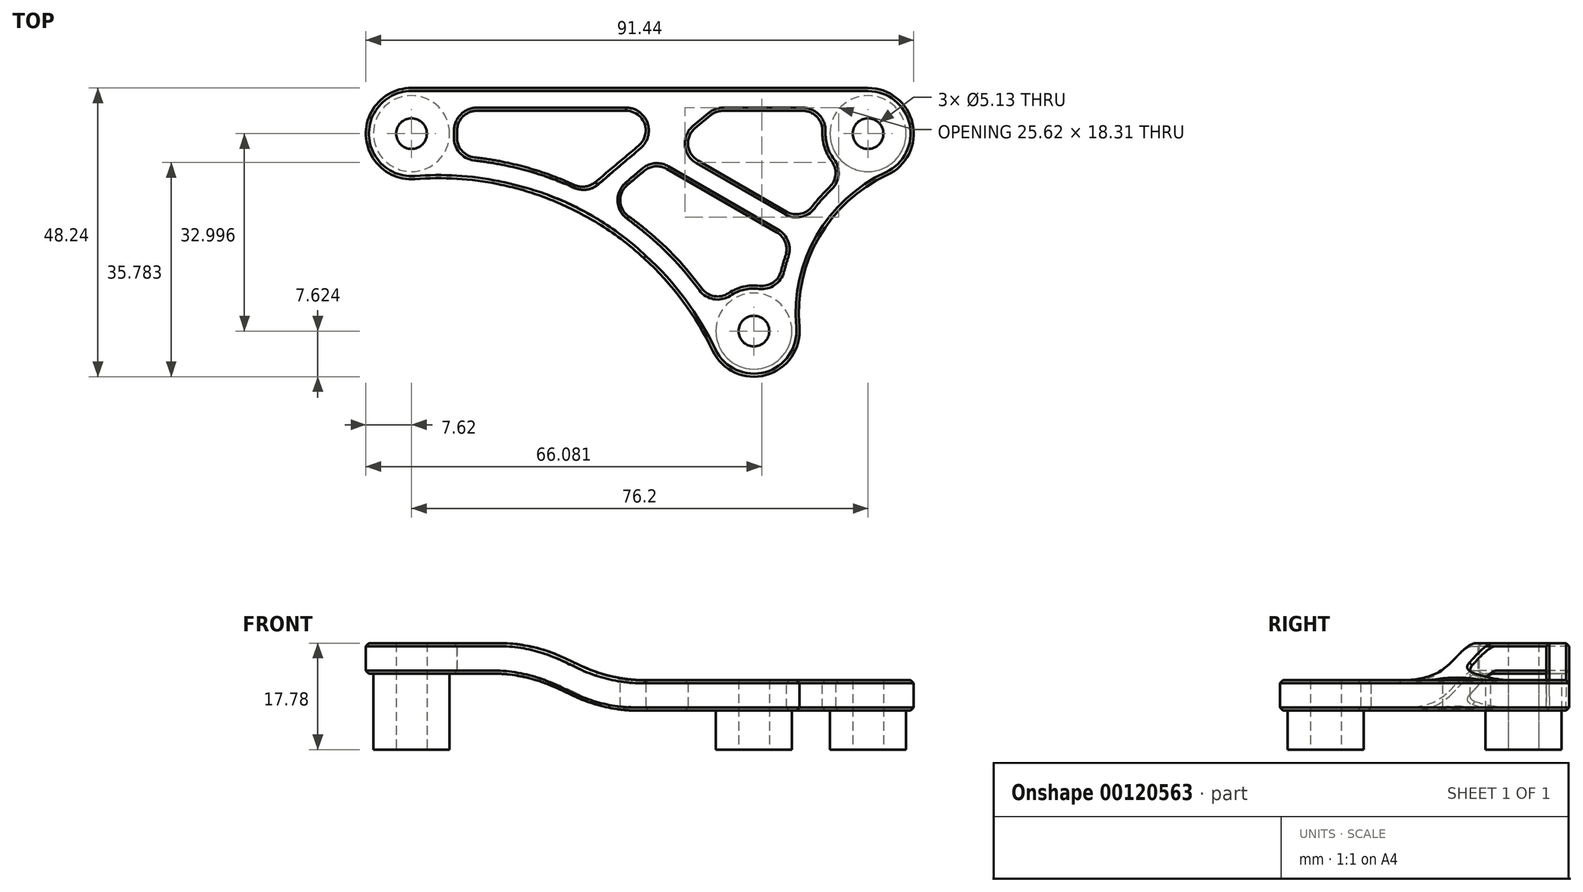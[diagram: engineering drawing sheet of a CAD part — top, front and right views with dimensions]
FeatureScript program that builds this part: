
annotation { "Feature Type Name" : "Feature", "Feature Type Description" : "" }
export const myFeature = defineFeature(function(context is Context, id is Id, definition is map)
    precondition{}
    {
        {
            var Q0;
            Q0=qCreatedBy(makeId("Top.planeOp"),FACE);
            var sketch = newSketch(context, id + "F0", { "sketchPlane" : qUnion([Q0])});
            skCircle(sketch, "E0", {"center": v(0, 0) * mm, "radius": 6.35 * mm});
            skCircle(sketch, "E1", {"center": v(76.2, 0) * mm, "radius": 6.35 * mm, "construction": true});
            skCircle(sketch, "E2", {"center": v(57.15, -33) * mm, "radius": 6.35 * mm, "construction": true});
            skLineSegment(sketch, "E3", {"start": v(0, 0) * mm, "end": v(76.2, 0) * mm, "construction": true});
            skLineSegment(sketch, "E4", {"start": v(57.15, -33) * mm, "end": v(76.2, 0) * mm, "construction": true});
            skSolve(sketch);
        }
        {
            var Q0;
            Q0 = qSketchRegion(id + "F0", true);
            extrude(context, id + "F1", {"entities" : qUnion([Q0]), "depth" : 17.78 * mm});
        }
        {
            var Q0;
            Q0=makeQuery(id+"F0.imprint","IMPRINT",FACE,{"disambiguationData":[TD([[makeQuery(id+"F0.imprint","IMPRINT",EDGE,{"derivedFrom":sQuery(id+"F0.wireOp",EDGE,"E0")}),1.0]])]});
            var sketch = newSketch(context, id + "F2", { "sketchPlane" : qUnion([Q0])});
            skCircle(sketch, "E5.0", {"center": v(76.2, 0) * mm, "radius": 6.35 * mm});
            skCircle(sketch, "E5.1", {"center": v(57.15, -33) * mm, "radius": 6.35 * mm});
            skSolve(sketch);
        }
        {
            var Q0;
            Q0 = qSketchRegion(id + "F2", true);
            extrude(context, id + "F3", {"entities" : qUnion([Q0]), "depth" : 7.62 * mm});
        }
        {
            var Q0;
            Q0=qCreatedBy(makeId("Front.planeOp"),FACE);
            var sketch = newSketch(context, id + "F4", { "sketchPlane" : qUnion([Q0])});
            skLineSegment(sketch, "E6", {"start": v(-12.8, 17.78) * mm, "end": v(20.18, 17.78) * mm});
            skLineSegment(sketch, "E7", {"start": v(84.3, 11.57) * mm, "end": v(33.5, 11.57) * mm});
            skLineSegment(sketch, "E8", {"start": v(20.18, 17.78) * mm, "end": v(33.5, 11.57) * mm});
            skLineSegment(sketch, "E9.0", {"start": v(84.3, 6.49) * mm, "end": v(32.37, 6.49) * mm});
            skLineSegment(sketch, "E9.1", {"start": v(19.05, 12.7) * mm, "end": v(32.37, 6.49) * mm});
            skLineSegment(sketch, "E9.2", {"start": v(-12.8, 12.7) * mm, "end": v(19.05, 12.7) * mm});
            skLineSegment(sketch, "E10", {"start": v(-12.8, 17.78) * mm, "end": v(-12.8, 12.7) * mm});
            skLineSegment(sketch, "E11", {"start": v(84.3, 6.49) * mm, "end": v(84.3, 11.57) * mm});
            skSolve(sketch);
        }
        {
            var Q0;
            Q0 = qSketchRegion(id + "F4", true);
            extrude(context, id + "F5", {"entities" : qUnion([Q0]), "operationType" : NewBodyOperationType.ADD, "depth" : 40.64 * mm, "hasSecondDirection" : true, "secondDirectionOppositeDirection" : true, "secondDirectionDepth" : 12.7 * mm});
        }
        {
            var Q0;
            Q0=qCreatedBy(makeId("Top.planeOp"),FACE);
            var sketch = newSketch(context, id + "F6", { "sketchPlane" : qUnion([Q0])});
            skArc(sketch, "E12", {"start": v(50.28, -36.29) * mm, "mid": v(29.87, -14.25) * mm, "end": v(0.58, -7.6) * mm});
            skArc(sketch, "E13", {"start": v(0, 7.62) * mm, "mid": v(-7.61, -0.3) * mm, "end": v(0.58, -7.6) * mm});
            skArc(sketch, "E14", {"start": v(50.28, -36.29) * mm, "mid": v(59.18, -40.34) * mm, "end": v(64.74, -32.3) * mm});
            skArc(sketch, "E15", {"start": v(79.4, -6.92) * mm, "mid": v(83.64, 1.63) * mm, "end": v(76.2, 7.62) * mm});
            skLineSegment(sketch, "E16", {"start": v(0, 7.62) * mm, "end": v(76.2, 7.62) * mm});
            skArc(sketch, "E17", {"start": v(79.4, -6.92) * mm, "mid": v(68.04, -17.28) * mm, "end": v(64.74, -32.3) * mm});
            skLineSegment(sketch, "E18.bottom", {"start": v(-19.2, 18.93) * mm, "end": v(108.25, 18.93) * mm});
            skLineSegment(sketch, "E18.top", {"start": v(-19.2, -48.45) * mm, "end": v(108.25, -48.45) * mm});
            skLineSegment(sketch, "E18.left", {"start": v(-19.2, 18.93) * mm, "end": v(-19.2, -48.45) * mm});
            skLineSegment(sketch, "E18.right", {"start": v(108.25, 18.93) * mm, "end": v(108.25, -48.45) * mm});
            skSolve(sketch);
        }
        {
            var Q0;
            Q0 = qSketchRegion(id + "F6", true);
            extrude(context, id + "F7", {"entities" : qUnion([Q0]), "operationType" : NewBodyOperationType.REMOVE, "depth" : 25.4 * mm});
        }
        {
            var Q0;
            Q0=makeQuery(id+"F5.opExtrude","SWEPT_EDGE",EDGE,{"disambiguationData":[OSD([sQuery(id+"F4.wireOp",EDGE,"E6"),sQuery(id+"F4.wireOp",EDGE,"E8")])]});
            var Q1;
            Q1=makeQuery(id+"F5.opExtrude","SWEPT_EDGE",EDGE,{"disambiguationData":[OSD([sQuery(id+"F4.wireOp",EDGE,"E7"),sQuery(id+"F4.wireOp",EDGE,"E8")])]});
            var Q2;
            Q2=makeQuery(id+"F5.opExtrude","SWEPT_EDGE",EDGE,{"disambiguationData":[OSD([sQuery(id+"F4.wireOp",EDGE,"E9.1"),sQuery(id+"F4.wireOp",EDGE,"E9.2")])]});
            var Q3;
            Q3=makeQuery(id+"F5.opExtrude","SWEPT_EDGE",EDGE,{"disambiguationData":[OSD([sQuery(id+"F4.wireOp",EDGE,"E9.0"),sQuery(id+"F4.wireOp",EDGE,"E9.1")])]});
            fillet(context, id + "F8", {"entities" : qUnion([Q0, Q1, Q2, Q3]), "radius" : 25.4 * mm, "tangentPropagation" : true, "allowEdgeOverflow" : false});
        }
        {
            var Q0;
            Q0=makeQuery(id+"F5.opExtrude","SWEPT_FACE",FACE,{"disambiguationData":[OSD([sQuery(id+"F4.wireOp",EDGE,"E7")])]});
            var sketch = newSketch(context, id + "F9", { "sketchPlane" : qUnion([Q0])});
            skLineSegment(sketch, "E19.0", {"start": v(13.03, 3.81) * mm, "end": v(6.6, 3.81) * mm});
            skLineSegment(sketch, "E19.1", {"start": v(13.03, 3.81) * mm, "end": v(26.18, 3.81) * mm});
            skLineSegment(sketch, "E19.2", {"start": v(27.04, 3.81) * mm, "end": v(26.18, 3.81) * mm});
            skArc(sketch, "E19.3", {"start": v(28.73, -9.32) * mm, "mid": v(28.88, -9.4) * mm, "end": v(29.04, -9.48) * mm});
            skArc(sketch, "E19.4", {"start": v(27.8, -8.88) * mm, "mid": v(28.27, -9.1) * mm, "end": v(28.73, -9.32) * mm});
            skArc(sketch, "E19.5", {"start": v(13.67, -4.42) * mm, "mid": v(20.9, -6.17) * mm, "end": v(27.8, -8.88) * mm});
            skArc(sketch, "E19.6", {"start": v(6.67, -3.68) * mm, "mid": v(10.18, -3.94) * mm, "end": v(13.67, -4.42) * mm});
            skArc(sketch, "E19.7", {"start": v(50.62, -29.06) * mm, "mid": v(42.65, -19.2) * mm, "end": v(32.61, -11.45) * mm});
            skArc(sketch, "E19.9", {"start": v(72.47, -6.64) * mm, "mid": v(68.48, -10.27) * mm, "end": v(65.23, -14.56) * mm});
            skLineSegment(sketch, "E19.11", {"start": v(40.18, 3.81) * mm, "end": v(44.87, 3.81) * mm});
            skLineSegment(sketch, "E19.12", {"start": v(27.04, 3.81) * mm, "end": v(40.18, 3.81) * mm});
            skArc(sketch, "E20", {"start": v(6.67, -3.68) * mm, "mid": v(7.62, 0.07) * mm, "end": v(6.6, 3.81) * mm});
            skArc(sketch, "E21", {"start": v(61.04, -26.44) * mm, "mid": v(55.3, -25.6) * mm, "end": v(50.62, -29.06) * mm});
            skArc(sketch, "E22", {"start": v(69.6, 3.81) * mm, "mid": v(68.85, -2.02) * mm, "end": v(72.47, -6.64) * mm});
            skLineSegment(sketch, "E23", {"start": v(44.87, 3.81) * mm, "end": v(29.04, -9.48) * mm});
            skLineSegment(sketch, "E24", {"start": v(50.8, 3.81) * mm, "end": v(43.71, -2.14) * mm});
            skLineSegment(sketch, "E25", {"start": v(43.71, -2.14) * mm, "end": v(65.23, -14.56) * mm});
            skLineSegment(sketch, "E26", {"start": v(40.6, -4.75) * mm, "end": v(63.43, -17.92) * mm});
            skCircle(sketch, "E27", {"center": v(64.27, -16.21) * mm, "radius": 1.9 * mm, "construction": true});
            skLineSegment(sketch, "E28.trimOffspring", {"start": v(50.8, 3.81) * mm, "end": v(69.6, 3.81) * mm});
            skLineSegment(sketch, "E29.trimOffspring", {"start": v(40.6, -4.75) * mm, "end": v(32.61, -11.45) * mm});
            skArc(sketch, "E30.trimOffspring", {"start": v(63.43, -17.92) * mm, "mid": v(61.9, -22.09) * mm, "end": v(61.04, -26.44) * mm});
            skLineSegment(sketch, "E31", {"start": v(65.23, -14.56) * mm, "end": v(64.27, -16.21) * mm, "construction": true});
            skLineSegment(sketch, "E32", {"start": v(64.27, -16.21) * mm, "end": v(63.43, -17.92) * mm, "construction": true});
            skSolve(sketch);
        }
        {
            var Q0;
            Q0 = qSketchRegion(id + "F9", true);
            extrude(context, id + "F10", {"entities" : qUnion([Q0]), "operationType" : NewBodyOperationType.REMOVE, "oppositeDirection" : true, "depth" : 25.4 * mm, "hasSecondDirection" : true, "secondDirectionOppositeDirection" : false, "secondDirectionDepth" : 25.4 * mm});
        }
        {
            var Q0;
            Q0=makeQuery(id+"F10.boolean.opBoolean","COPY",EDGE,{"derivedFrom":makeQuery(id+"F10.opExtrude","SWEPT_EDGE",EDGE,{"disambiguationData":[OSD([sQuery(id+"F9.wireOp",EDGE,"E19.0"),sQuery(id+"F9.wireOp",EDGE,"E20")])]})});
            var Q1;
            Q1=makeQuery(id+"F10.boolean.opBoolean","COPY",EDGE,{"derivedFrom":makeQuery(id+"F10.opExtrude","SWEPT_EDGE",EDGE,{"disambiguationData":[OSD([sQuery(id+"F9.wireOp",EDGE,"E19.6"),sQuery(id+"F9.wireOp",EDGE,"E20")])]})});
            var Q2;
            Q2=makeQuery(id+"F10.boolean.opBoolean","COPY",EDGE,{"derivedFrom":makeQuery(id+"F10.opExtrude","SWEPT_EDGE",EDGE,{"disambiguationData":[OSD([sQuery(id+"F9.wireOp",EDGE,"E19.11"),sQuery(id+"F9.wireOp",EDGE,"E23")])]})});
            var Q3;
            Q3=makeQuery(id+"F10.boolean.opBoolean","COPY",EDGE,{"derivedFrom":makeQuery(id+"F10.opExtrude","SWEPT_EDGE",EDGE,{"disambiguationData":[OSD([sQuery(id+"F9.wireOp",EDGE,"E22"),sQuery(id+"F9.wireOp",EDGE,"E28.trimOffspring")])]})});
            var Q4;
            Q4=makeQuery(id+"F10.boolean.opBoolean","COPY",EDGE,{"derivedFrom":makeQuery(id+"F10.opExtrude","SWEPT_EDGE",EDGE,{"disambiguationData":[OSD([sQuery(id+"F9.wireOp",EDGE,"E19.9"),sQuery(id+"F9.wireOp",EDGE,"E22")])]})});
            var Q5;
            Q5=makeQuery(id+"F10.boolean.opBoolean","COPY",EDGE,{"derivedFrom":makeQuery(id+"F10.opExtrude","SWEPT_EDGE",EDGE,{"disambiguationData":[OSD([sQuery(id+"F9.wireOp",EDGE,"E19.9"),sQuery(id+"F9.wireOp",EDGE,"E25")])]})});
            var Q6;
            Q6=makeQuery(id+"F10.boolean.opBoolean","COPY",EDGE,{"derivedFrom":makeQuery(id+"F10.opExtrude","SWEPT_EDGE",EDGE,{"disambiguationData":[OSD([sQuery(id+"F9.wireOp",EDGE,"E21"),sQuery(id+"F9.wireOp",EDGE,"E30.trimOffspring")])]})});
            var Q7;
            Q7=makeQuery(id+"F10.boolean.opBoolean","COPY",EDGE,{"derivedFrom":makeQuery(id+"F10.opExtrude","SWEPT_EDGE",EDGE,{"disambiguationData":[OSD([sQuery(id+"F9.wireOp",EDGE,"E26"),sQuery(id+"F9.wireOp",EDGE,"E30.trimOffspring")])]})});
            var Q8;
            Q8=makeQuery(id+"F10.boolean.opBoolean","COPY",EDGE,{"derivedFrom":makeQuery(id+"F10.opExtrude","SWEPT_EDGE",EDGE,{"disambiguationData":[OSD([sQuery(id+"F9.wireOp",EDGE,"E26"),sQuery(id+"F9.wireOp",EDGE,"E29.trimOffspring")])]})});
            var Q9;
            Q9=makeQuery(id+"F10.boolean.opBoolean","COPY",EDGE,{"derivedFrom":makeQuery(id+"F10.opExtrude","SWEPT_EDGE",EDGE,{"disambiguationData":[OSD([sQuery(id+"F9.wireOp",EDGE,"E24"),sQuery(id+"F9.wireOp",EDGE,"E28.trimOffspring")])]})});
            var Q10;
            Q10=makeQuery(id+"F10.boolean.opBoolean","COPY",EDGE,{"derivedFrom":makeQuery(id+"F10.opExtrude","SWEPT_EDGE",EDGE,{"disambiguationData":[OSD([sQuery(id+"F9.wireOp",EDGE,"E19.7"),sQuery(id+"F9.wireOp",EDGE,"E29.trimOffspring")])]})});
            var Q11;
            Q11=makeQuery(id+"F10.boolean.opBoolean","COPY",EDGE,{"derivedFrom":makeQuery(id+"F10.opExtrude","SWEPT_EDGE",EDGE,{"disambiguationData":[OSD([sQuery(id+"F9.wireOp",EDGE,"E19.7"),sQuery(id+"F9.wireOp",EDGE,"E21")])]})});
            var Q12;
            Q12=makeQuery(id+"F10.boolean.opBoolean","COPY",EDGE,{"derivedFrom":makeQuery(id+"F10.opExtrude","SWEPT_EDGE",EDGE,{"disambiguationData":[OSD([sQuery(id+"F9.wireOp",EDGE,"E19.3"),sQuery(id+"F9.wireOp",EDGE,"E23")])]})});
            var Q13;
            Q13=makeQuery(id+"F10.boolean.opBoolean","COPY",EDGE,{"derivedFrom":makeQuery(id+"F10.opExtrude","SWEPT_EDGE",EDGE,{"disambiguationData":[OSD([sQuery(id+"F9.wireOp",EDGE,"E24"),sQuery(id+"F9.wireOp",EDGE,"E25")])]})});
            fillet(context, id + "F11", {"entities" : qUnion([Q0, Q1, Q2, Q3, Q4, Q5, Q6, Q7, Q8, Q9, Q10, Q11, Q12, Q13]), "radius" : 3.3 * mm, "tangentPropagation" : true, "allowEdgeOverflow" : false});
        }
        {
            var Q0;
            Q0=makeQuery(id+"F7.boolean.opBoolean","INTERSECT",EDGE,{"derivedFrom":[makeQuery(id+"F5.boolean.opBoolean","MERGE",FACE,{"derivedFrom":[makeQuery(id+"F1.opExtrude","CAP_FACE",FACE,{"disambiguationData":[OSD([sQuery(id+"F0.wireOp",EDGE,"E0")])],"isStart":false}),makeQuery(id+"F5.opExtrude","SWEPT_FACE",FACE,{"disambiguationData":[OSD([sQuery(id+"F4.wireOp",EDGE,"E6")])]})]}),makeQuery(id+"F7.opExtrude","SWEPT_FACE",FACE,{"disambiguationData":[OSD([sQuery(id+"F6.wireOp",EDGE,"E16")])]})]});
            var Q1;
            Q1=makeQuery(id+"F10.boolean.opBoolean","INTERSECT",EDGE,{"derivedFrom":[makeQuery(id+"F8.opFillet","BLEND_FACE",FACE,{"disambiguationData":[OSD([sQuery(id+"F4.wireOp",EDGE,"E6"),sQuery(id+"F4.wireOp",EDGE,"E8")])]}),makeQuery(id+"F10.opExtrude","SWEPT_FACE",FACE,{"disambiguationData":[OSD([sQuery(id+"F9.wireOp",EDGE,"E19.0"),sQuery(id+"F9.wireOp",EDGE,"E19.1"),sQuery(id+"F9.wireOp",EDGE,"E19.2"),sQuery(id+"F9.wireOp",EDGE,"E19.11"),sQuery(id+"F9.wireOp",EDGE,"E19.12")])]})]});
            var Q2;
            Q2=makeQuery(id+"F10.boolean.opBoolean","INTERSECT",EDGE,{"derivedFrom":[makeQuery(id+"F5.opExtrude","SWEPT_FACE",FACE,{"disambiguationData":[OSD([sQuery(id+"F4.wireOp",EDGE,"E7")])]}),makeQuery(id+"F10.opExtrude","SWEPT_FACE",FACE,{"disambiguationData":[OSD([sQuery(id+"F9.wireOp",EDGE,"E24")])]})]});
            var Q3;
            Q3=makeQuery(id+"F10.boolean.opBoolean","INTERSECT",EDGE,{"derivedFrom":[makeQuery(id+"F5.opExtrude","SWEPT_FACE",FACE,{"disambiguationData":[OSD([sQuery(id+"F4.wireOp",EDGE,"E7")])]}),makeQuery(id+"F10.opExtrude","SWEPT_FACE",FACE,{"disambiguationData":[OSD([sQuery(id+"F9.wireOp",EDGE,"E29.trimOffspring")])]})]});
            var Q4;
            Q4=makeQuery(id+"F10.boolean.opBoolean","INTERSECT",EDGE,{"derivedFrom":[makeQuery(id+"F8.opFillet","BLEND_FACE",FACE,{"disambiguationData":[OSD([sQuery(id+"F4.wireOp",EDGE,"E7"),sQuery(id+"F4.wireOp",EDGE,"E8")])]}),makeQuery(id+"F10.opExtrude","SWEPT_FACE",FACE,{"disambiguationData":[OSD([sQuery(id+"F9.wireOp",EDGE,"E29.trimOffspring")])]})]});
            chamfer(context, id + "F12", {"entities" : qUnion([Q0, Q1, Q2, Q3, Q4]), "width" : 0.5 * mm, "tangentPropagation" : true});
        }
        {
            var Q0;
            Q0=makeQuery(id+"F10.boolean.opBoolean","INTERSECT",EDGE,{"derivedFrom":[makeQuery(id+"F5.opExtrude","SWEPT_FACE",FACE,{"disambiguationData":[OSD([sQuery(id+"F4.wireOp",EDGE,"E9.0")])]}),makeQuery(id+"F10.opExtrude","SWEPT_FACE",FACE,{"disambiguationData":[OSD([sQuery(id+"F9.wireOp",EDGE,"E19.7")])]})]});
            var Q1;
            Q1=makeQuery(id+"F10.boolean.opBoolean","INTERSECT",EDGE,{"derivedFrom":[makeQuery(id+"F8.opFillet","BLEND_FACE",FACE,{"disambiguationData":[OSD([sQuery(id+"F4.wireOp",EDGE,"E9.0"),sQuery(id+"F4.wireOp",EDGE,"E9.1")])]}),makeQuery(id+"F10.opExtrude","SWEPT_FACE",FACE,{"disambiguationData":[OSD([sQuery(id+"F9.wireOp",EDGE,"E23")])]})]});
            var Q2;
            Q2=makeQuery(id+"F10.boolean.opBoolean","INTERSECT",EDGE,{"derivedFrom":[makeQuery(id+"F5.opExtrude","SWEPT_FACE",FACE,{"disambiguationData":[OSD([sQuery(id+"F4.wireOp",EDGE,"E9.0")])]}),makeQuery(id+"F10.opExtrude","SWEPT_FACE",FACE,{"disambiguationData":[OSD([sQuery(id+"F9.wireOp",EDGE,"E25")])]})]});
            var Q3;
            Q3=makeQuery(id+"F7.boolean.opBoolean","INTERSECT",EDGE,{"derivedFrom":[makeQuery(id+"F5.opExtrude","SWEPT_FACE",FACE,{"disambiguationData":[OSD([sQuery(id+"F4.wireOp",EDGE,"E9.0")])]}),makeQuery(id+"F7.opExtrude","SWEPT_FACE",FACE,{"disambiguationData":[OSD([sQuery(id+"F6.wireOp",EDGE,"E16")])]})]});
            chamfer(context, id + "F13", {"entities" : qUnion([Q0, Q1, Q2, Q3]), "width" : 0.5 * mm, "tangentPropagation" : true});
        }
        {
            var Q0;
            Q0=makeQuery(id+"F2.imprint","IMPRINT",FACE,{"disambiguationData":[TD([[makeQuery(id+"F2.imprint","IMPRINT",EDGE,{"derivedFrom":makeQuery(id+"F0.imprint","IMPRINT",EDGE,{"derivedFrom":sQuery(id+"F0.wireOp",EDGE,"E0")})}),1.0]])]});
            var sketch = newSketch(context, id + "F14", { "sketchPlane" : qUnion([Q0])});
            skCircle(sketch, "E33", {"center": v(0, 0) * mm, "radius": 2.57 * mm});
            skCircle(sketch, "E34", {"center": v(57.15, -33) * mm, "radius": 2.57 * mm});
            skCircle(sketch, "E35", {"center": v(76.2, 0) * mm, "radius": 2.57 * mm});
            skSolve(sketch);
        }
        {
            var Q0;
            Q0 = qSketchRegion(id + "F14", true);
            extrude(context, id + "F15", {"entities" : qUnion([Q0]), "operationType" : NewBodyOperationType.REMOVE, "depth" : 25.4 * mm});
        }
    });
